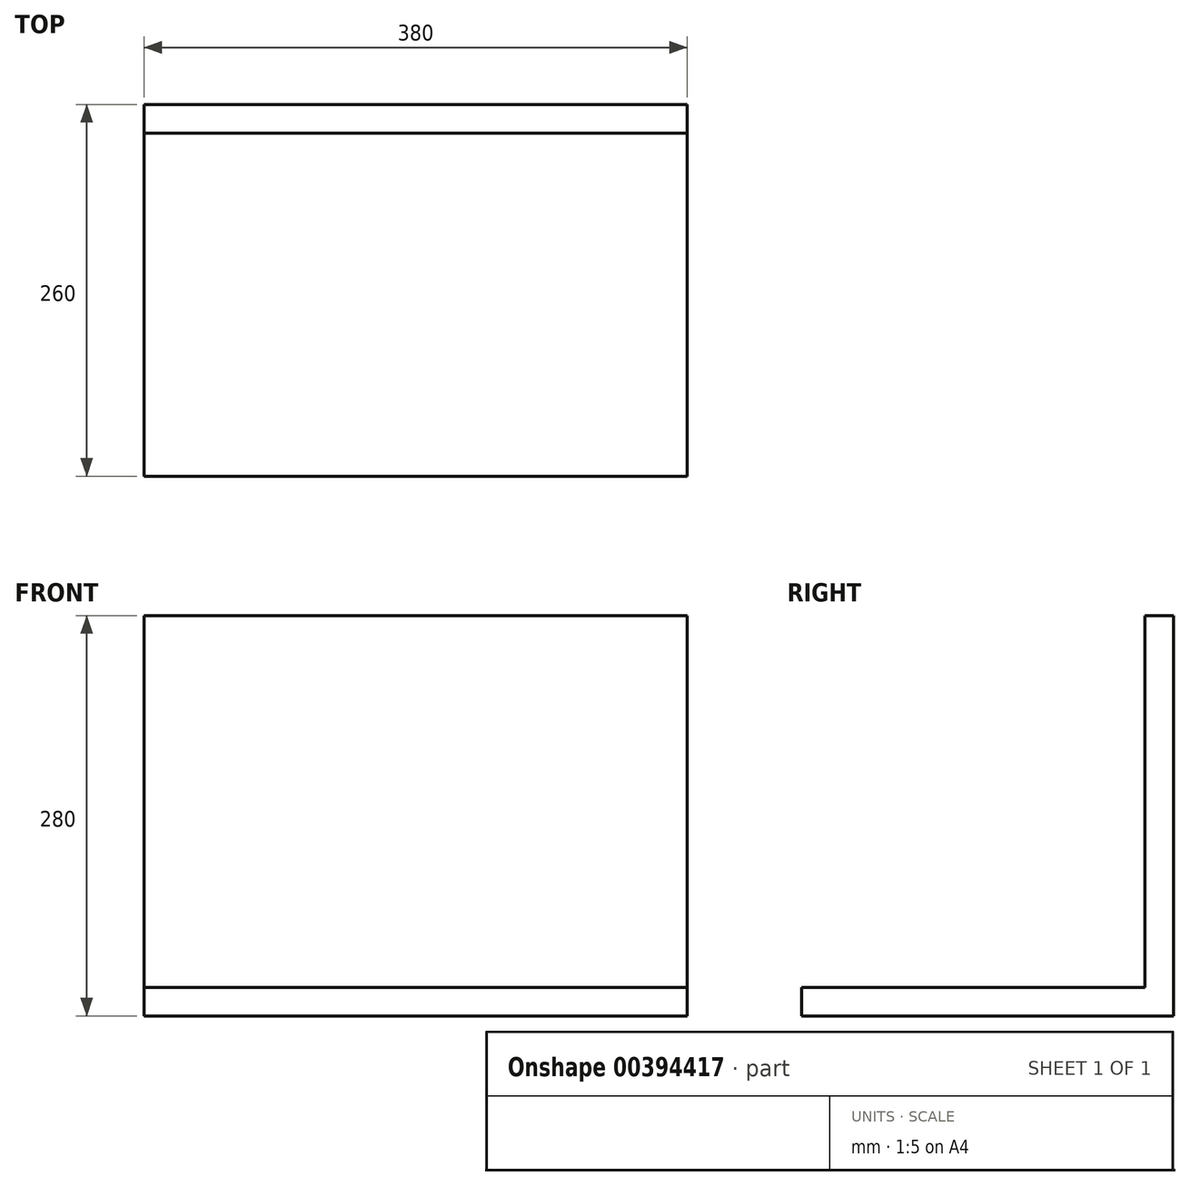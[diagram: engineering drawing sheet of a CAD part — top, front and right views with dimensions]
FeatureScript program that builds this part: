
annotation { "Feature Type Name" : "Feature", "Feature Type Description" : "" }
export const myFeature = defineFeature(function(context is Context, id is Id, definition is map)
    precondition{}
    {
        {
            var Q0;
            Q0=qCreatedBy(makeId("Top.planeOp"),FACE);
            var sketch = newSketch(context, id + "F0", { "sketchPlane" : qUnion([Q0])});
            skLineSegment(sketch, "E0.bottom", {"start": v(-380, 0) * mm, "end": v(0, 0) * mm});
            skLineSegment(sketch, "E0.right", {"start": v(0, 0) * mm, "end": v(0, 260) * mm});
            skLineSegment(sketch, "E1", {"start": v(0, 260) * mm, "end": v(-380, 260) * mm});
            skLineSegment(sketch, "E2", {"start": v(-380, 0) * mm, "end": v(-380, 260) * mm});
            skSolve(sketch);
        }
        {
            var Q0;
            Q0=makeQuery(id+"F0.imprint","IMPRINT",FACE,{"disambiguationData":[TD([[makeQuery(id+"F0.imprint","IMPRINT",EDGE,{"derivedFrom":sQuery(id+"F0.wireOp",EDGE,"E0.bottom")}),1.0]])]});
            extrude(context, id + "F1", {"entities" : qUnion([Q0]), "depth" : 20 * mm, "offsetDistance" : 25 * mm});
        }
        {
            var Q0;
            Q0=makeQuery(id+"F1.opExtrude","CAP_FACE",FACE,{"disambiguationData":[OSD([sQuery(id+"F0.wireOp",EDGE,"E0.bottom"),sQuery(id+"F0.wireOp",EDGE,"E0.top"),sQuery(id+"F0.wireOp",EDGE,"E0.left"),sQuery(id+"F0.wireOp",EDGE,"E0.right")])],"isStart":false});
            var sketch = newSketch(context, id + "F2", { "sketchPlane" : qUnion([Q0])});
            skLineSegment(sketch, "E3.bottom", {"start": v(-380, 260) * mm, "end": v(0, 260) * mm});
            skLineSegment(sketch, "E3.top", {"start": v(-380, 240) * mm, "end": v(0, 240) * mm});
            skLineSegment(sketch, "E3.left", {"start": v(-380, 260) * mm, "end": v(-380, 240) * mm});
            skLineSegment(sketch, "E3.right", {"start": v(0, 260) * mm, "end": v(0, 240) * mm});
            skSolve(sketch);
        }
        {
            var Q0;
            Q0=makeQuery(id+"F2.imprint","IMPRINT",FACE,{"disambiguationData":[TD([[makeQuery(id+"F2.imprint","IMPRINT",EDGE,{"derivedFrom":sQuery(id+"F2.wireOp",EDGE,"E3.bottom")}),1.0]])]});
            extrude(context, id + "F3", {"entities" : qUnion([Q0]), "operationType" : NewBodyOperationType.ADD, "depth" : 260 * mm, "offsetDistance" : 25 * mm});
        }
    });
